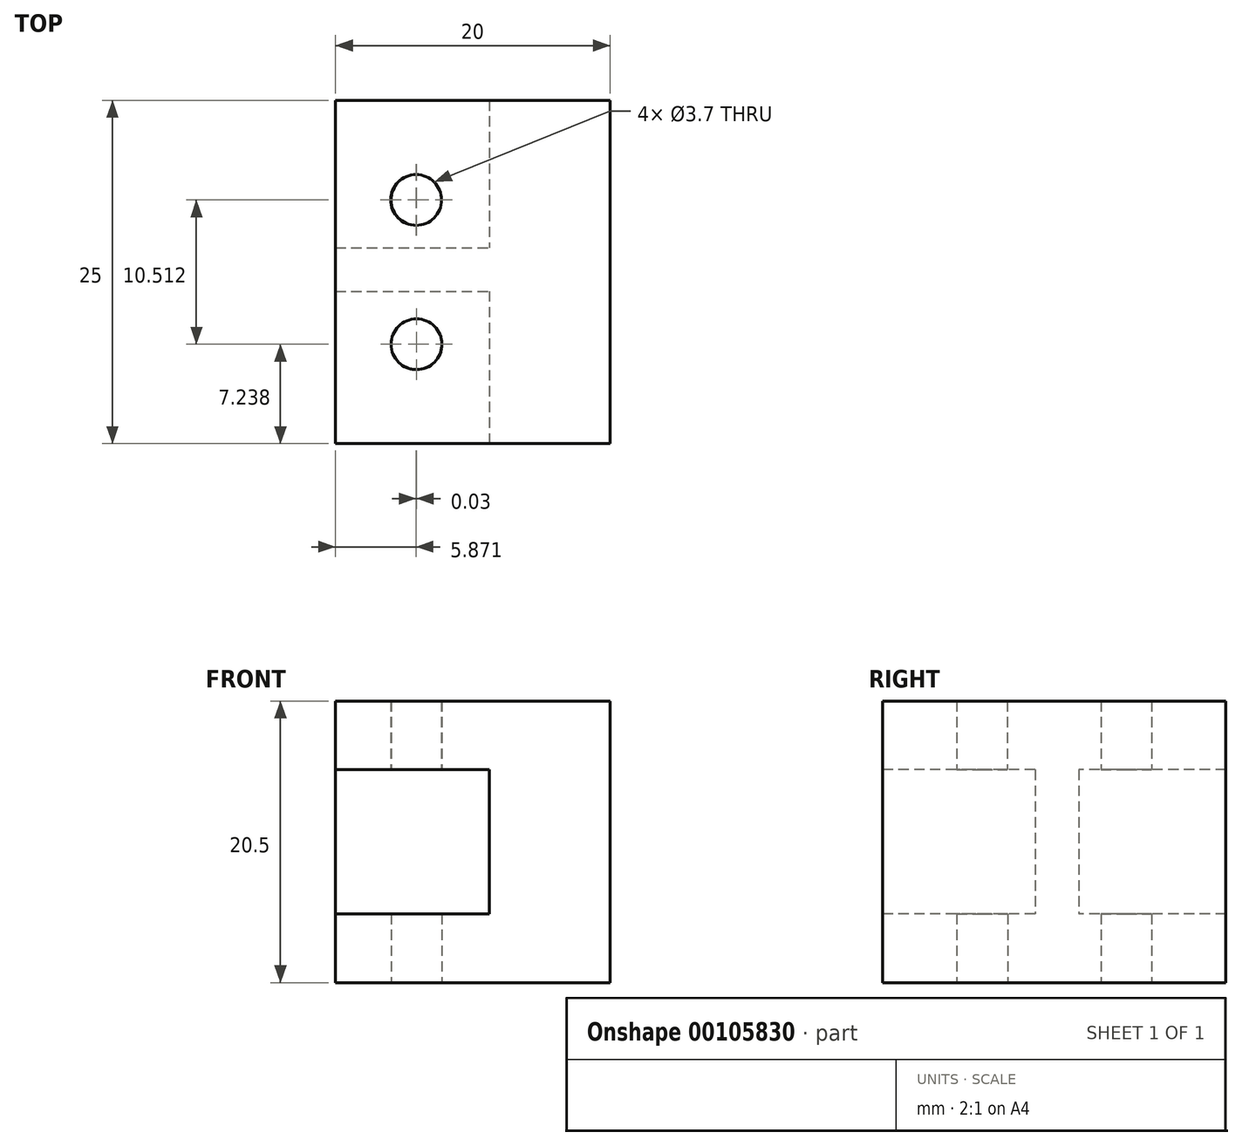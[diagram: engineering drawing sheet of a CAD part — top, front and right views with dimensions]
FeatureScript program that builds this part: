
annotation { "Feature Type Name" : "Feature", "Feature Type Description" : "" }
export const myFeature = defineFeature(function(context is Context, id is Id, definition is map)
    precondition{}
    {
        {
            var Q0;
            Q0=qCreatedBy(makeId("Top.planeOp"),FACE);
            var sketch = newSketch(context, id + "F0", { "sketchPlane" : qUnion([Q0])});
            skLineSegment(sketch, "E0.bottom", {"start": v(-27.2, 7.25) * mm, "end": v(-7.2, 7.25) * mm});
            skLineSegment(sketch, "E0.top", {"start": v(-27.2, -17.75) * mm, "end": v(-7.2, -17.75) * mm});
            skLineSegment(sketch, "E0.left", {"start": v(-27.2, 7.25) * mm, "end": v(-27.2, -17.75) * mm});
            skLineSegment(sketch, "E0.right", {"start": v(-7.2, 7.25) * mm, "end": v(-7.2, -17.75) * mm});
            skCircle(sketch, "E1", {"center": v(-21.3, 0) * mm, "radius": 1.85 * mm});
            skCircle(sketch, "E2", {"center": v(-21.3, -10.5) * mm, "radius": 1.85 * mm});
            skSolve(sketch);
        }
        {
            var Q0;
            Q0=qSketchRegion(id+"F0",true);
            extrude(context, id + "F1", {"entities" : qUnion([Q0]), "depth" : 5 * mm});
        }
        {
            var Q0;
            Q0=makeQuery(id+"F1.opExtrude","CAP_FACE",FACE,{"disambiguationData":[OSD([sQuery(id+"F0.wireOp",EDGE,"E0.bottom"),sQuery(id+"F0.wireOp",EDGE,"E0.top"),sQuery(id+"F0.wireOp",EDGE,"E0.left"),sQuery(id+"F0.wireOp",EDGE,"E0.right"),sQuery(id+"F0.wireOp",EDGE,"E1"),sQuery(id+"F0.wireOp",EDGE,"E2")])],"isStart":false});
            var sketch = newSketch(context, id + "F2", { "sketchPlane" : qUnion([Q0])});
            skLineSegment(sketch, "E3.bottom", {"start": v(-7.2, 7.25) * mm, "end": v(-15.99, 7.25) * mm});
            skLineSegment(sketch, "E3.top", {"start": v(-7.2, -17.75) * mm, "end": v(-15.99, -17.75) * mm});
            skLineSegment(sketch, "E3.left", {"start": v(-7.2, 7.25) * mm, "end": v(-7.2, -17.75) * mm});
            skLineSegment(sketch, "E3.right", {"start": v(-15.99, 7.25) * mm, "end": v(-15.99, -17.75) * mm});
            skLineSegment(sketch, "E4.bottom", {"start": v(-27.2, -3.47) * mm, "end": v(-15.99, -3.47) * mm});
            skLineSegment(sketch, "E4.top", {"start": v(-27.2, -6.65) * mm, "end": v(-15.99, -6.65) * mm});
            skLineSegment(sketch, "E4.left", {"start": v(-27.2, -3.47) * mm, "end": v(-27.2, -6.65) * mm});
            skLineSegment(sketch, "E4.right", {"start": v(-15.99, -3.47) * mm, "end": v(-15.99, -6.65) * mm});
            skSolve(sketch);
        }
        {
            var Q0;
            Q0=makeQuery(id+"F2.imprint","IMPRINT",FACE,{"disambiguationData":[TD([[makeQuery(id+"F2.imprint","IMPRINT",EDGE,{"derivedFrom":sQuery(id+"F2.wireOp",EDGE,"E4.bottom")}),-1.0]])]});
            var Q1;
            {var subQ1=sQuery(id+"F2.wireOp",EDGE,"E3.bottom");Q1=makeQuery(id+"F2.imprint","IMPRINT",FACE,{"disambiguationData":[TD([[makeQuery(id+"F2.imprint","IMPRINT",EDGE,{"derivedFrom":subQ1}),-1.0]])]});}
            var Q2;
            Q2=sQuery(id+"F2.wireOp",EDGE,"E4.left");
            var Q3;
            Q3=sQuery(id+"F2.wireOp",EDGE,"E4.top");
            var Q4;
            Q4=sQuery(id+"F2.wireOp",EDGE,"E4.bottom");
            var Q5;
            Q5=sQuery(id+"F2.wireOp",EDGE,"E3.right");
            extrude(context, id + "F3", {"entities" : qUnion([Q0, Q1]), "operationType" : NewBodyOperationType.ADD, "surfaceEntities" : qUnion([Q2, Q3, Q4, Q5]), "depth" : 10.5 * mm});
        }
        {
            var Q0;
            Q0=makeQuery(id+"F3.opExtrude","CAP_FACE",FACE,{"disambiguationData":[OSD([sQuery(id+"F2.wireOp",EDGE,"E3.bottom"),sQuery(id+"F2.wireOp",EDGE,"E3.top"),sQuery(id+"F2.wireOp",EDGE,"E3.left"),sQuery(id+"F2.wireOp",EDGE,"E3.right"),sQuery(id+"F2.wireOp",EDGE,"E4.bottom"),sQuery(id+"F2.wireOp",EDGE,"E4.top"),sQuery(id+"F2.wireOp",EDGE,"E4.left")])],"isStart":false});
            var sketch = newSketch(context, id + "F4", { "sketchPlane" : qUnion([Q0])});
            skLineSegment(sketch, "E5.bottom", {"start": v(-7.2, 7.25) * mm, "end": v(-27.2, 7.25) * mm});
            skLineSegment(sketch, "E5.top", {"start": v(-7.2, -17.75) * mm, "end": v(-27.2, -17.75) * mm});
            skLineSegment(sketch, "E5.left", {"start": v(-7.2, 7.25) * mm, "end": v(-7.2, -17.75) * mm});
            skLineSegment(sketch, "E5.right", {"start": v(-27.2, 7.25) * mm, "end": v(-27.2, -17.75) * mm});
            skCircle(sketch, "E6", {"center": v(-21.33, 0) * mm, "radius": 1.85 * mm});
            skCircle(sketch, "E7", {"center": v(-21.3, -10.51) * mm, "radius": 1.85 * mm});
            skSolve(sketch);
        }
        {
            var Q0;
            Q0 = qSketchRegion(id + "F4", true);
            extrude(context, id + "F5", {"entities" : qUnion([Q0]), "operationType" : NewBodyOperationType.ADD, "depth" : 5 * mm});
        }
    });
